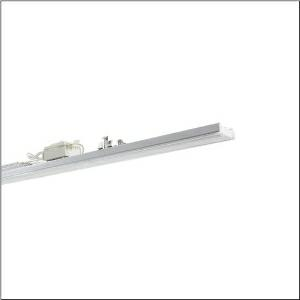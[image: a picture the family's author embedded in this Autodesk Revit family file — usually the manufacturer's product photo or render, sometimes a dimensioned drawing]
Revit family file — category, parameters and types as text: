
# Revit family: licross_21_recessed_mo_52tl19cn485g
name_source: partatom
category: Lighting Fixtures
units: mm (PartAtom-declared; Revit-internal decimal feet)

## family parameters
Cut with Voids When Loaded = No
Host = Face
Light Source = No
Part Type = Normal
Room Calculation Point = No
Round Connector Dimension = Use Diameter
Shared = No

## types (1)
- --- (1 x LED, 8870 lm, 49.9 W, 4000K)
    Apparent Load = 50 VA
    CIE Flux Codes = 55 90 98 100 100
    Color Rendering = 80
    Color Temperature = 4000K
    Default Elevation = 1800 mm
    Description = Licross 21 Recessed MO, luminaire insert, of sheet steel, galvanised, coil coated, white, length: 1.500mm, width: 66mm, height: 67mm, LED rated luminous flux: 8.880lm, light colour: 840, SDCM (Standard Deviation of Colour Matching)MacAdam ≤ 3 SDCM (initial), control gear: ON/OFF Multilumen, CLOi, with plug, 5-pole, with phase selection, mains connection: 220..240V, AC, 50/60Hz, start of lifetime: 50W, end of service life: 61W, internal wiring halogen-free, primary light control with lens, of plastic, primary optical cover: cover, of PMMA, light emission: direct distribution, primary light characteristic: double asymmetric, protection rating (complete): IP40, insulation class (complete): insulation class I (protective earthing), certification: CE, ENEC, VDE, UKCA, protection symbol: D if used in an environment without relevant dust loads with corresponding accessories, impact resistance: IK06, permissible ambient temperature for indoor applications: -35..+40°C, corresponds to IFS (International Featured Standards) requirements for safety and quality in the food industry, reducing of maximum allowable ambient temperature of 5°C with ceiling mounting, LABS conformity tested according to VDMA 24364:2018-05, The light source and the operating device comply with the requirements of the Ecodesign Regulation (EU) 2019/2020 and are replaceable in accordance with this regulation, packaging unit: 1 piece
    Height = 58 mm
    Lamp = 1 x LED
    Lamp Light Flux = 8870 lm
    Lamp Power = 49.9 W
    Lamp count = 1
    Length = 1500 mm
    Luminous efficacy = 178 lm/W
    Manufacturer = Siteco
    ModVariant = No
    Model = 52TL19CN485G
    Mounting Place = Ceiling
    Mounting Type = Pendant
    Number of Poles = 1
    OnlyDefault = Yes
    Power Factor = 1
    Product Name = Licross 21 Recessed MO
    Product group = luminaire insert | ceiling pendant
    ProductGroupID = 901
    Protection Class = Protection class I
    Protection Degree = IP 40
    RLX_Detail_Level = 1
    RLX_Emergency_Light_Flux = 0 lm
    RLX_Emergency_Type = 0
    RLX_Emergency_Type_DB = No
    RlxData = <blob elided: 22597 chars, md5=4dfaefd3>
    Socket = socket
    Standby Power = 0 W
    System Light Flux = 8870 lm
    System Power = 50 W
    Type Comments = factory setting: luminous flux: 100 % | (A | C | E) | 116 mA
    Type Image = l_1296930.jpg
    URL = http://relux.com
    VarID = @adj_110761
    Voltage = 0 V
    Weight = 0.00 kg
    Width = 66 mm

## geometry (parser evidence)
native form markers: Blend x4, Sweep x11
no freeform markers — native parametric forms only
